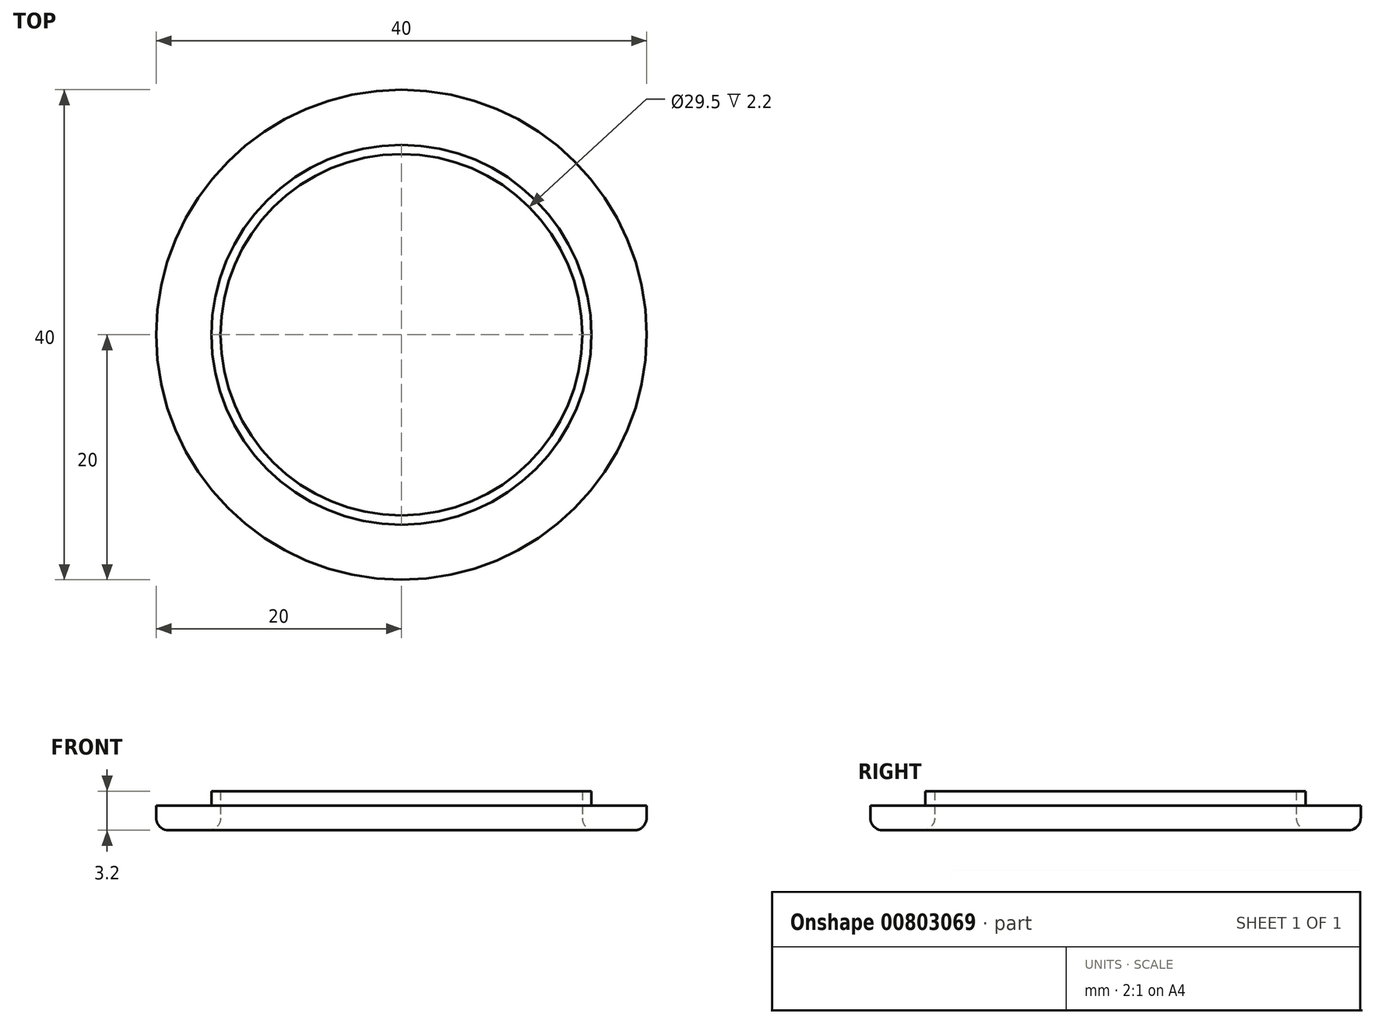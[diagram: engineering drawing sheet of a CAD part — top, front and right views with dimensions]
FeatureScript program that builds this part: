
annotation { "Feature Type Name" : "Feature", "Feature Type Description" : "" }
export const myFeature = defineFeature(function(context is Context, id is Id, definition is map)
    precondition{}
    {
        {
            var Q0;
            Q0=qCreatedBy(makeId("Top.planeOp"),FACE);
            var sketch = newSketch(context, id + "F0", { "sketchPlane" : qUnion([Q0])});
            skCircle(sketch, "E0", {"center": v(0, 0) * mm, "radius": 20 * mm});
            skCircle(sketch, "E1", {"center": v(0, 0) * mm, "radius": 15.5 * mm});
            skSolve(sketch);
        }
        {
            var Q0;
            Q0=makeQuery(id+"F0.imprint","IMPRINT",FACE,{"disambiguationData":[TD([[makeQuery(id+"F0.imprint","IMPRINT",EDGE,{"derivedFrom":sQuery(id+"F0.wireOp",EDGE,"E0")}),1.0]])]});
            extrude(context, id + "F1", {"entities" : qUnion([Q0]), "depth" : 2 * mm, "offsetDistance" : 25 * mm});
        }
        {
            var Q0;
            Q0=qCreatedBy(makeId("Top.planeOp"),FACE);
            var sketch = newSketch(context, id + "F2", { "sketchPlane" : qUnion([Q0])});
            skCircle(sketch, "E2", {"center": v(0, 0) * mm, "radius": 14.75 * mm});
            skCircle(sketch, "E3", {"center": v(0, 0) * mm, "radius": 15.5 * mm});
            skSolve(sketch);
        }
        {
            var Q0;
            Q0=makeQuery(id+"F2.imprint","IMPRINT",FACE,{"disambiguationData":[TD([[makeQuery(id+"F2.imprint","IMPRINT",EDGE,{"derivedFrom":sQuery(id+"F2.wireOp",EDGE,"E2")}),-1.0]])]});
            extrude(context, id + "F3", {"entities" : qUnion([Q0]), "operationType" : NewBodyOperationType.ADD, "depth" : 3.2 * mm, "offsetDistance" : 25 * mm});
        }
        {
            var Q0;
            Q0=makeQuery(id+"F1.opExtrude","CAP_EDGE",EDGE,{"disambiguationData":[OSD([sQuery(id+"F0.wireOp",EDGE,"E0")])],"isStart":true});
            var Q1;
            Q1=makeQuery(id+"F3.opExtrude","CAP_EDGE",EDGE,{"disambiguationData":[OSD([sQuery(id+"F2.wireOp",EDGE,"E2")])],"isStart":true});
            fillet(context, id + "F4", {"entities" : qUnion([Q0, Q1]), "radius" : 1 * mm, "tangentPropagation" : true, "allowEdgeOverflow" : false});
        }
    });
